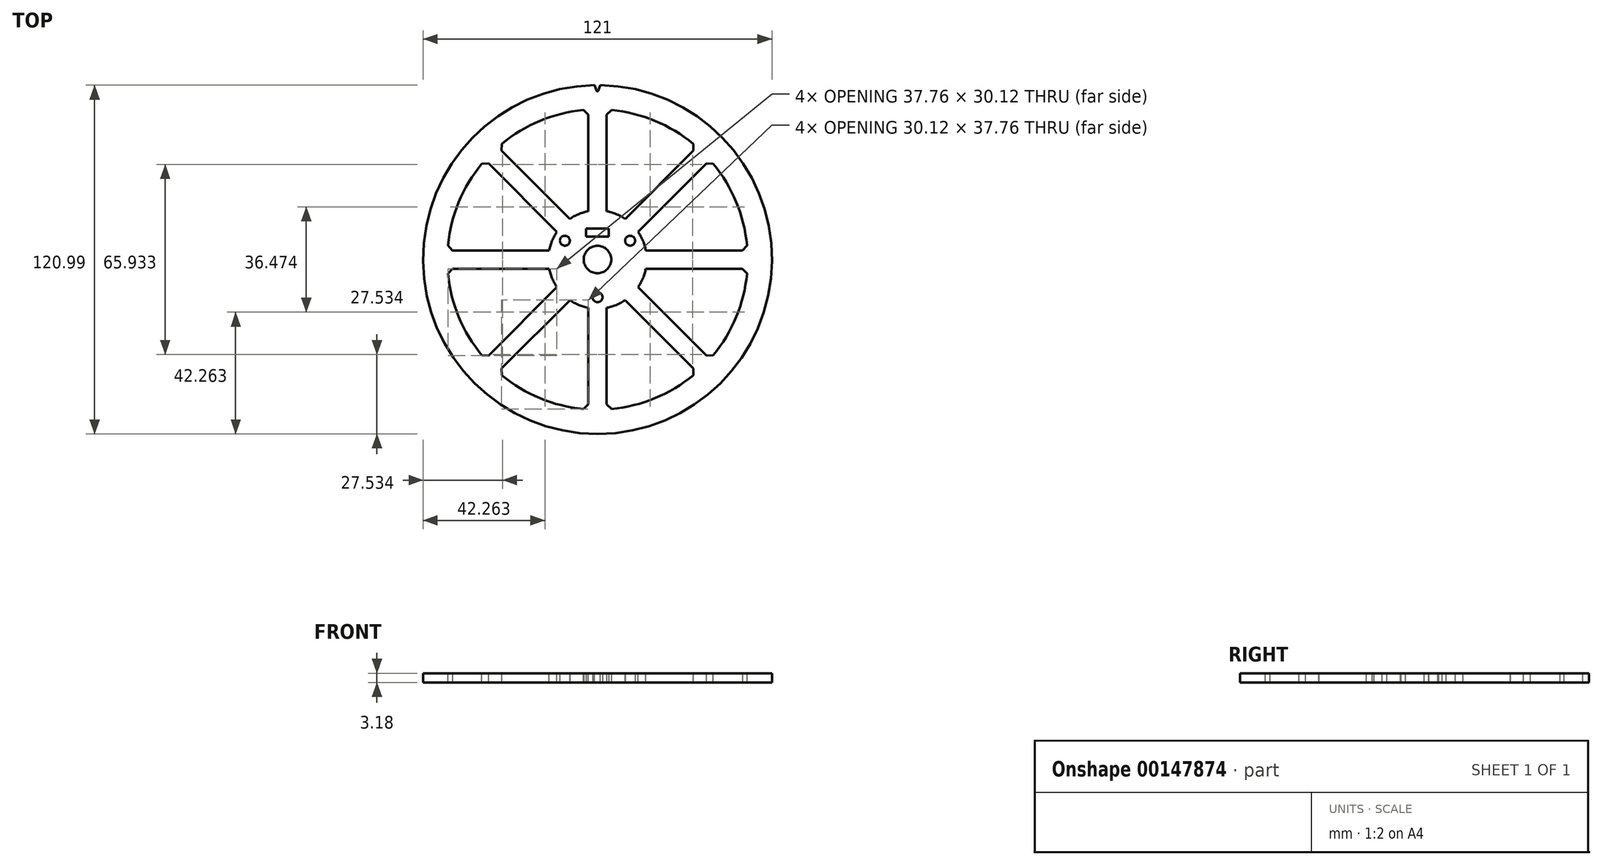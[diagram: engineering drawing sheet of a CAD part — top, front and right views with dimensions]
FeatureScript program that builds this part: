
annotation { "Feature Type Name" : "Feature", "Feature Type Description" : "" }
export const myFeature = defineFeature(function(context is Context, id is Id, definition is map)
    precondition{}
    {
        {
            var Q0;
            Q0=qCreatedBy(makeId("Top.planeOp"),FACE);
            var sketch = newSketch(context, id + "F0", { "sketchPlane" : qUnion([Q0])});
            skCircle(sketch, "E0", {"center": v(0, 0) * mm, "radius": 60.5 * mm});
            skCircle(sketch, "E1", {"center": v(0, 0) * mm, "radius": 4.76 * mm});
            skCircle(sketch, "E2", {"center": v(0, 0) * mm, "radius": 17.04 * mm, "construction": true});
            skCircle(sketch, "E3.cCircle", {"center": v(0, 0) * mm, "radius": 6.54 * mm, "construction": true});
            skLineSegment(sketch, "E3.0", {"start": v(-11.32, 6.54) * mm, "end": v(11.32, 6.54) * mm, "construction": true});
            skLineSegment(sketch, "E3.1", {"start": v(11.32, 6.54) * mm, "end": v(0, -13.07) * mm, "construction": true});
            skLineSegment(sketch, "E3.2", {"start": v(0, -13.07) * mm, "end": v(-11.32, 6.54) * mm, "construction": true});
            skPoint(sketch, "E3.0.midPoint", {"position": v(0, 6.54) * mm});
            skCircle(sketch, "E4", {"center": v(-11.32, 6.54) * mm, "radius": 3.97 * mm, "construction": true});
            skCircle(sketch, "E5", {"center": v(-11.32, 6.54) * mm, "radius": 1.73 * mm});
            skCircle(sketch, "E6", {"center": v(11.32, 6.54) * mm, "radius": 1.73 * mm});
            skCircle(sketch, "E7", {"center": v(0, -13.07) * mm, "radius": 1.73 * mm});
            skLineSegment(sketch, "E8", {"start": v(0, 0) * mm, "end": v(0, 4.76) * mm, "construction": true});
            skLineSegment(sketch, "E9", {"start": v(0, 4.76) * mm, "end": v(0, 7.94) * mm, "construction": true});
            skLineSegment(sketch, "E10.bottom", {"start": v(-3.94, 10.78) * mm, "end": v(3.94, 10.78) * mm});
            skLineSegment(sketch, "E10.top", {"start": v(-3.94, 7.94) * mm, "end": v(3.94, 7.94) * mm});
            skLineSegment(sketch, "E10.left", {"start": v(-3.94, 10.78) * mm, "end": v(-3.94, 7.94) * mm});
            skLineSegment(sketch, "E10.right", {"start": v(3.94, 10.78) * mm, "end": v(3.94, 7.94) * mm});
            skSolve(sketch);
        }
        {
            var Q0;
            Q0=makeQuery(id+"F0.imprint","IMPRINT",FACE,{"disambiguationData":[TD([[makeQuery(id+"F0.imprint","IMPRINT",EDGE,{"derivedFrom":sQuery(id+"F0.wireOp",EDGE,"d7zeTPih-CRss-xDOh-gPdP-rmPCdwzH7cdN.left")}),1.0]])]});
            var Q1;
            Q1=makeQuery(id+"F0.imprint","IMPRINT",FACE,{"disambiguationData":[TD([[makeQuery(id+"F0.imprint","IMPRINT",EDGE,{"derivedFrom":sQuery(id+"F0.wireOp",EDGE,"E0")}),1.0]])]});
            extrude(context, id + "F1", {"entities" : qUnion([Q0, Q1]), "depth" : 3.17 * mm});
        }
        {
            var Q0;
            Q0=makeQuery(id+"F1.opExtrude","CAP_FACE",FACE,{"disambiguationData":[OSD([sQuery(id+"F0.wireOp",EDGE,"d7zeTPih-CRss-xDOh-gPdP-rmPCdwzH7cdN.left"),sQuery(id+"F0.wireOp",EDGE,"d7zeTPih-CRss-xDOh-gPdP-rmPCdwzH7cdN.right"),sQuery(id+"F0.wireOp",EDGE,"ScfBMfkV-s1yN-Ls9R-SGr5-fEyGpD6zak8e"),sQuery(id+"F0.wireOp",EDGE,"xnxmVwjl-FvSF-m7sj-be2U-u85gZZGoORGZ"),sQuery(id+"F0.wireOp",EDGE,"E0")])],"isStart":false});
            var sketch = newSketch(context, id + "F2", { "sketchPlane" : qUnion([Q0])});
            skLineSegment(sketch, "E11", {"start": v(0, 0) * mm, "end": v(0, 60.5) * mm, "construction": true});
            skLineSegment(sketch, "E12", {"start": v(0, 0) * mm, "end": v(0.66, 60.5) * mm, "construction": true});
            skArc(sketch, "E13", {"start": v(1.02, 60.5) * mm, "mid": v(0, 60.5) * mm, "end": v(-1.02, 60.5) * mm});
            skLineSegment(sketch, "E14", {"start": v(-1.02, 60.5) * mm, "end": v(-0.28, 58.52) * mm});
            skLineSegment(sketch, "E15", {"start": v(1.02, 60.5) * mm, "end": v(0.28, 58.52) * mm});
            skPoint(sketch, "E16", {"position": v(0.65, 59.5) * mm});
            skArc(sketch, "E17", {"start": v(-0.28, 58.52) * mm, "mid": v(0, 58.33) * mm, "end": v(0.28, 58.52) * mm});
            skSolve(sketch);
        }
        {
            var Q0;
            Q0=qSketchRegion(id+"F2",true);
            var Q1;
            Q1=makeQuery(id+"F1.opExtrude","CAP_FACE",FACE,{"disambiguationData":[OSD([sQuery(id+"F0.wireOp",EDGE,"d7zeTPih-CRss-xDOh-gPdP-rmPCdwzH7cdN.left"),sQuery(id+"F0.wireOp",EDGE,"d7zeTPih-CRss-xDOh-gPdP-rmPCdwzH7cdN.right"),sQuery(id+"F0.wireOp",EDGE,"ScfBMfkV-s1yN-Ls9R-SGr5-fEyGpD6zak8e"),sQuery(id+"F0.wireOp",EDGE,"xnxmVwjl-FvSF-m7sj-be2U-u85gZZGoORGZ"),sQuery(id+"F0.wireOp",EDGE,"E0")])],"isStart":true});
            extrude(context, id + "F3", {"entities" : qUnion([Q0]), "operationType" : NewBodyOperationType.REMOVE, "endBound" : BoundingType.UP_TO_SURFACE, "oppositeDirection" : true, "endBoundEntityFace" : qUnion([Q1]), "depth" : 25.4 * mm});
        }
        {
            var Q0;
            Q0=makeQuery(id+"F1.opExtrude","CAP_FACE",FACE,{"disambiguationData":[OSD([sQuery(id+"F0.wireOp",EDGE,"E0"),sQuery(id+"F0.wireOp",EDGE,"E1"),sQuery(id+"F0.wireOp",EDGE,"tRzARMfv-7BFj-HnuO-QooS-YK2TcsRHxJGM"),sQuery(id+"F0.wireOp",EDGE,"l2f0ixeT-HVOn-P7pL-0EBq-9Ms4uDoOWkmK"),sQuery(id+"F0.wireOp",EDGE,"czIBXI4K-ms6v-gZLf-gVDV-WxWQWUw0xqfL"),sQuery(id+"F0.wireOp",EDGE,"zD3yCDk3-du4V-XvNA-neFI-n9ijwsGpr5Hr")])],"isStart":false});
            var sketch = newSketch(context, id + "F4", { "sketchPlane" : qUnion([Q0])});
            skLineSegment(sketch, "E18", {"start": v(0, 0) * mm, "end": v(0, 16.75) * mm, "construction": true});
            skLineSegment(sketch, "E19", {"start": v(0, 16.75) * mm, "end": v(3.18, 16.75) * mm, "construction": true});
            skLineSegment(sketch, "E20", {"start": v(3.18, 16.75) * mm, "end": v(3.18, 51.98) * mm});
            skLineSegment(sketch, "E21", {"start": v(3.18, 51.98) * mm, "end": v(0, 51.98) * mm, "construction": true});
            skLineSegment(sketch, "E22", {"start": v(0, 51.98) * mm, "end": v(0, 58.33) * mm, "construction": true});
            skCircle(sketch, "E23", {"center": v(0, 0) * mm, "radius": 58.33 * mm, "construction": true});
            skArc(sketch, "E24", {"start": v(9.6, 14.09) * mm, "mid": v(6.52, 15.75) * mm, "end": v(3.18, 16.75) * mm});
            skLineSegment(sketch, "E25", {"start": v(0, 0) * mm, "end": v(11.84, 11.84) * mm, "construction": true});
            skLineSegment(sketch, "E26", {"start": v(11.84, 11.84) * mm, "end": v(9.6, 14.09) * mm, "construction": true});
            skLineSegment(sketch, "E27", {"start": v(9.6, 14.09) * mm, "end": v(34.51, 39) * mm});
            skArc(sketch, "E28", {"start": v(34.51, 39) * mm, "mid": v(19.93, 48.11) * mm, "end": v(3.17, 51.98) * mm});
            skSolve(sketch);
        }
        {
            var Q0;
            Q0=qSketchRegion(id+"F4",true);
            var Q1;
            Q1=makeQuery(id+"F1.opExtrude","SWEPT_BODY",BODY,{"disambiguationData":[OSD([sQuery(id+"F0.wireOp",EDGE,"E0"),sQuery(id+"F0.wireOp",EDGE,"E1"),sQuery(id+"F0.wireOp",EDGE,"tRzARMfv-7BFj-HnuO-QooS-YK2TcsRHxJGM"),sQuery(id+"F0.wireOp",EDGE,"l2f0ixeT-HVOn-P7pL-0EBq-9Ms4uDoOWkmK"),sQuery(id+"F0.wireOp",EDGE,"czIBXI4K-ms6v-gZLf-gVDV-WxWQWUw0xqfL"),sQuery(id+"F0.wireOp",EDGE,"zD3yCDk3-du4V-XvNA-neFI-n9ijwsGpr5Hr")])]});
            extrude(context, id + "F5", {"entities" : qUnion([Q0]), "operationType" : NewBodyOperationType.REMOVE, "endBound" : BoundingType.UP_TO_BODY, "oppositeDirection" : true, "endBoundEntityBody" : qUnion([Q1]), "depth" : 25.4 * mm});
        }
        {
            var Q0;
            Q0=makeQuery(id+"F5.boolean.opBoolean","COPY",EDGE,{"derivedFrom":makeQuery(id+"F5.opExtrude","SWEPT_EDGE",EDGE,{"disambiguationData":[OSD([sQuery(id+"F4.wireOp",EDGE,"E20"),sQuery(id+"F4.wireOp",EDGE,"E28")])]})});
            var Q1;
            Q1=makeQuery(id+"F5.boolean.opBoolean","COPY",EDGE,{"derivedFrom":makeQuery(id+"F5.opExtrude","SWEPT_EDGE",EDGE,{"disambiguationData":[OSD([sQuery(id+"F4.wireOp",EDGE,"E27"),sQuery(id+"F4.wireOp",EDGE,"E28")])]})});
            chamfer(context, id + "F6", {"entities" : qUnion([Q0, Q1]), "width" : 1.59 * mm, "tangentPropagation" : true});
        }
        {
            var Q0;
            Q0=makeQuery(id+"F5.boolean.opBoolean","COPY",FACE,{"derivedFrom":makeQuery(id+"F5.opExtrude","SWEPT_FACE",FACE,{"disambiguationData":[OSD([sQuery(id+"F4.wireOp",EDGE,"E24")])]})});
            var Q1;
            Q1=makeQuery(id+"F5.boolean.opBoolean","COPY",FACE,{"derivedFrom":makeQuery(id+"F5.opExtrude","SWEPT_FACE",FACE,{"disambiguationData":[OSD([sQuery(id+"F4.wireOp",EDGE,"E20")])]})});
            var Q2;
            Q2=makeQuery(id+"F5.boolean.opBoolean","COPY",FACE,{"derivedFrom":makeQuery(id+"F5.opExtrude","SWEPT_FACE",FACE,{"disambiguationData":[OSD([sQuery(id+"F4.wireOp",EDGE,"E27")])]})});
            var Q3;
            Q3=makeQuery(id+"F6.opChamfer","BLEND_FACE",FACE,{"disambiguationData":[OSD([sQuery(id+"F4.wireOp",EDGE,"E27"),sQuery(id+"F4.wireOp",EDGE,"E28")])]});
            var Q4;
            Q4=makeQuery(id+"F5.boolean.opBoolean","COPY",FACE,{"derivedFrom":makeQuery(id+"F5.opExtrude","SWEPT_FACE",FACE,{"disambiguationData":[OSD([sQuery(id+"F4.wireOp",EDGE,"E28")])]})});
            var Q5;
            Q5=makeQuery(id+"F6.opChamfer","BLEND_FACE",FACE,{"disambiguationData":[OSD([sQuery(id+"F4.wireOp",EDGE,"E20"),sQuery(id+"F4.wireOp",EDGE,"E28")])]});
            var Q6;
            Q6=makeQuery(id+"F1.opExtrude","SWEPT_FACE",FACE,{"disambiguationData":[OSD([sQuery(id+"F0.wireOp",EDGE,"E1")])]});
            circularPattern(context, id + "F7", {"patternType" : PatternType.FACE, "faces" : qUnion([Q0, Q1, Q2, Q3, Q4, Q5]), "axis" : qUnion([Q6]), "angle" : 45 * degree, "instanceCount" : 8});
        }
    });
